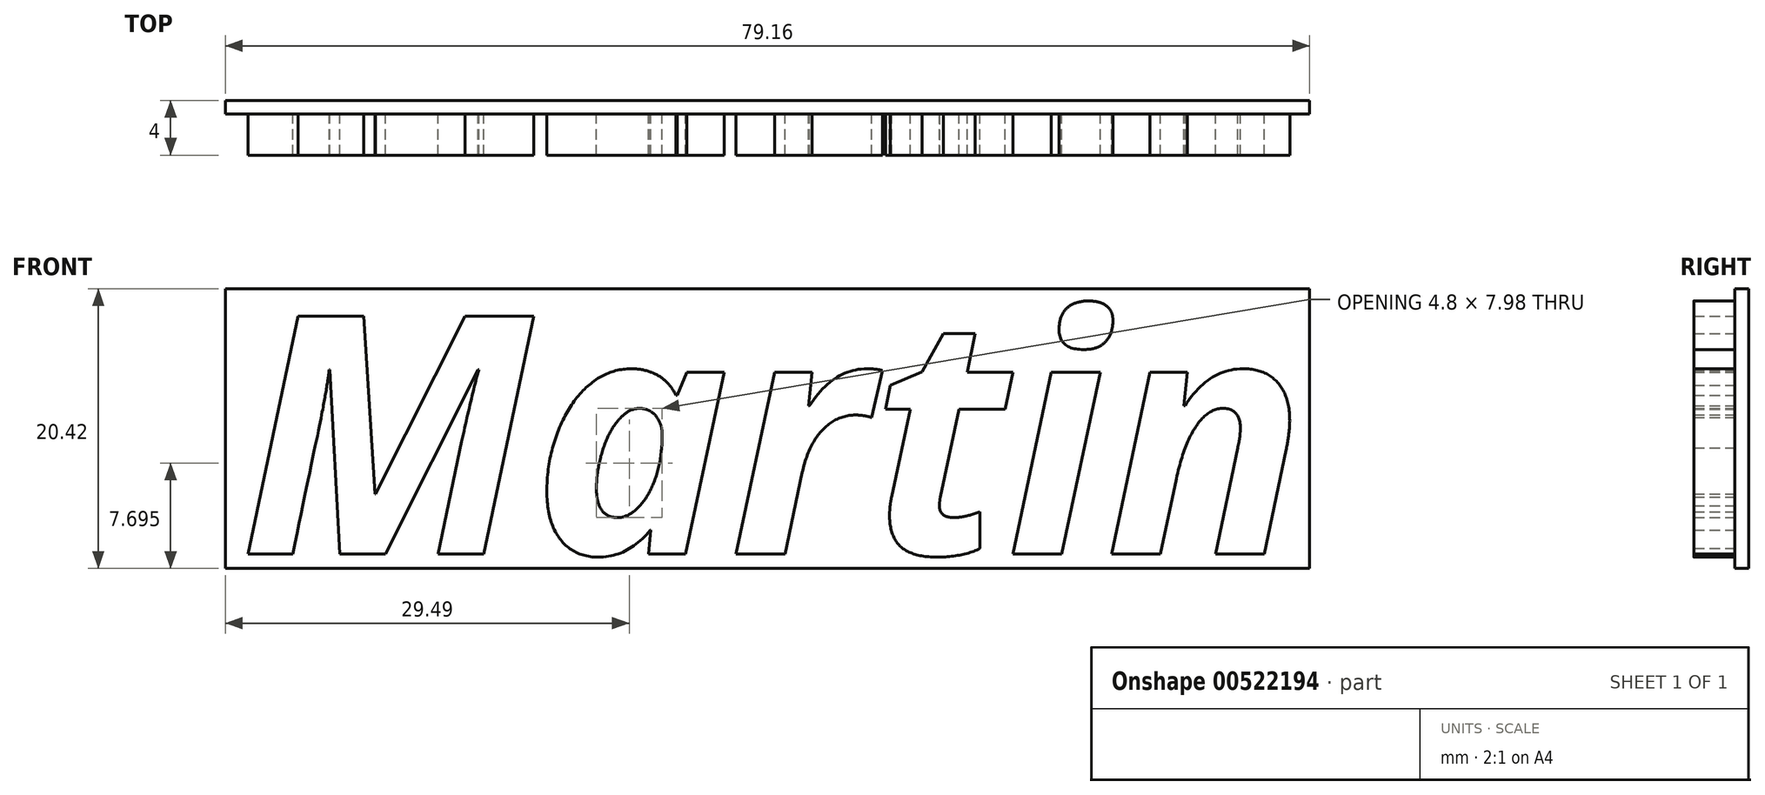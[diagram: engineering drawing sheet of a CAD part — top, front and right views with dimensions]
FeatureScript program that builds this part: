
annotation { "Feature Type Name" : "Feature", "Feature Type Description" : "" }
export const myFeature = defineFeature(function(context is Context, id is Id, definition is map)
    precondition{}
    {
        {
            var Q0;
            Q0=qCreatedBy(makeId("Front.planeOp"),FACE);
            var sketch = newSketch(context, id + "F0", { "sketchPlane" : qUnion([Q0])});
            skText(sketch, "E0", { "text": "Martin", "fontName": "OpenSans-BoldItalic.ttf"});
            const initialGuessF0  = {"E0": [-0.04475, -0.00012, 1, 0, 0.0175]};
            skSetInitialGuess(sketch, initialGuessF0);
            skSolve(sketch);
        }
        {
            var Q0;
            Q0=qSketchRegion(id+"F0",true);
            extrude(context, id + "F1", {"entities" : qUnion([Q0]), "depth" : 3 * mm});
        }
        {
            var Q0;
            Q0=makeQuery(id+"F0.imprint","IMPRINT",FACE,{"disambiguationData":[TD([[makeQuery(id+"F0.imprint","IMPRINT",EDGE,{"derivedFrom":sQuery(id+"F0.wireOp",EDGE,"E0.sketch_text.stroke-36")}),-1.0]])]});
            var sketch = newSketch(context, id + "F2", { "sketchPlane" : qUnion([Q0])});
            skLineSegment(sketch, "E1.bottom", {"start": v(-45.77, 19.24) * mm, "end": v(33.39, 19.24) * mm});
            skLineSegment(sketch, "E1.top", {"start": v(-45.77, -1.18) * mm, "end": v(33.39, -1.18) * mm});
            skLineSegment(sketch, "E1.left", {"start": v(-45.77, 19.24) * mm, "end": v(-45.77, -1.18) * mm});
            skLineSegment(sketch, "E1.right", {"start": v(33.39, 19.24) * mm, "end": v(33.39, -1.18) * mm});
            skSolve(sketch);
        }
        {
            var Q0;
            Q0=qSketchRegion(id+"F2",true);
            extrude(context, id + "F3", {"entities" : qUnion([Q0]), "oppositeDirection" : true, "depth" : 1 * mm, "offsetDistance" : 25 * mm});
        }
    });
